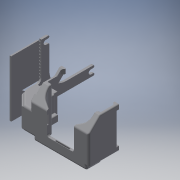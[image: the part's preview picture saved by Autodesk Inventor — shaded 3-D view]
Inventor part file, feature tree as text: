
AUTODESK INVENTOR PART (.ipt)
format: ipt  version: 2016 (Build 200138000, 138)  size: 1,285,120 bytes
history: native  units: in
note: dims shown in document units (in); Inventor stores cm internally (conversion verified against a paired STEP export)
features: extrude x9, sketch x9, fillet x6, other x1, plane x1, pattern_linear x1, imported_body x1
ambient origin geometry x8: Origin, YZ Plane, XZ Plane, XY Plane, X Axis, Y Axis, Z Axis, Center Point
bodies: Solid1 (feature_tree)
feature tree (28):
  other  "uploads-a6-b2-57-75-86-ReplicatorFanDuct21"
  extrude  "Extrusion1"  Depth=0.1in TaperAngle=0.0deg
  fillet  "Fillet1"  Radius=0.1969in
  extrude  "Extrusion2"  Depth=1.3126in
  fillet  "Fillet2"  Radius=0.1in
  extrude  "Extrusion4"  Depth=0.1575in
  fillet  "Fillet3"  Radius=1.5748in
  extrude  "Extrusion5"  Depth=0.0787in
  fillet  "Fillet4"  Radius=0.1575in
  fillet  "Fillet5"  Radius=0.0787in
  plane  "Work Plane1"
  extrude  "Extrusion7"  Depth=0.0787in
  extrude  "Extrusion8"  Depth=0.1969in
  pattern_linear  "Rectangular Pattern1"  Spacing1=0.0591in  [1 undecoded]
  extrude  "Extrusion9"  Depth=0.0394in
  extrude  "Extrusion10"  Depth=0.0394in
  extrude  "Extrusion12"  Depth=0.0394in TaperAngle=0.0deg
  fillet  "Fillet6"  Radius=0.05in
  imported_body  "Base1"
  sketch  "Sketch1"  dims[d0=0.4331in d1=0.1in d2=0.0in d3=0.1969in]
  sketch  "Sketch2"  dims[d4=0.2756in d5=1.3126in d6=0.1in d7=0.0in]
  sketch  "Sketch4"  dims[d8=0.1575in d13=0.315in d14=1.5748in]
  sketch  "Sketch6"  dims[d15=0.1in d16=0.0in d17=0.5906in d19=0.1575in d20=0.0787in]
  sketch  "Sketch8"  dims[d21=0.0787in d22=0.0787in]
  sketch  "Sketch9"  dims[d23=0.1969in d24=0.1969in]
  sketch  "Sketch10"  dims[d25=0.1in d26=0.0in]
  sketch  "Sketch11"  dims[d27=0.0394in]
  sketch  "Sketch13"  dims[d28=0.0394in d34=0.0591in d35=0.0984in d36=0.0591in d37=0.05in d38=0.0in d39=0.05in d40=0.0in d41=4.7244in d43=0.0984in d44=1.1811in d46=0.1181in d47=0.3937in d49=0.3937in d51=0.05in d52=0.0in d53=0.05in d54=0.0in d58=0.0157in d59=0.0394in d60=0.3937in d61=0.0in d62=0.0394in]
note: 1 required parameter value undecoded (feature->parameter linkage not recoverable at this tier; creation-order binding heuristic only, values carry confidence <= 0.55)
